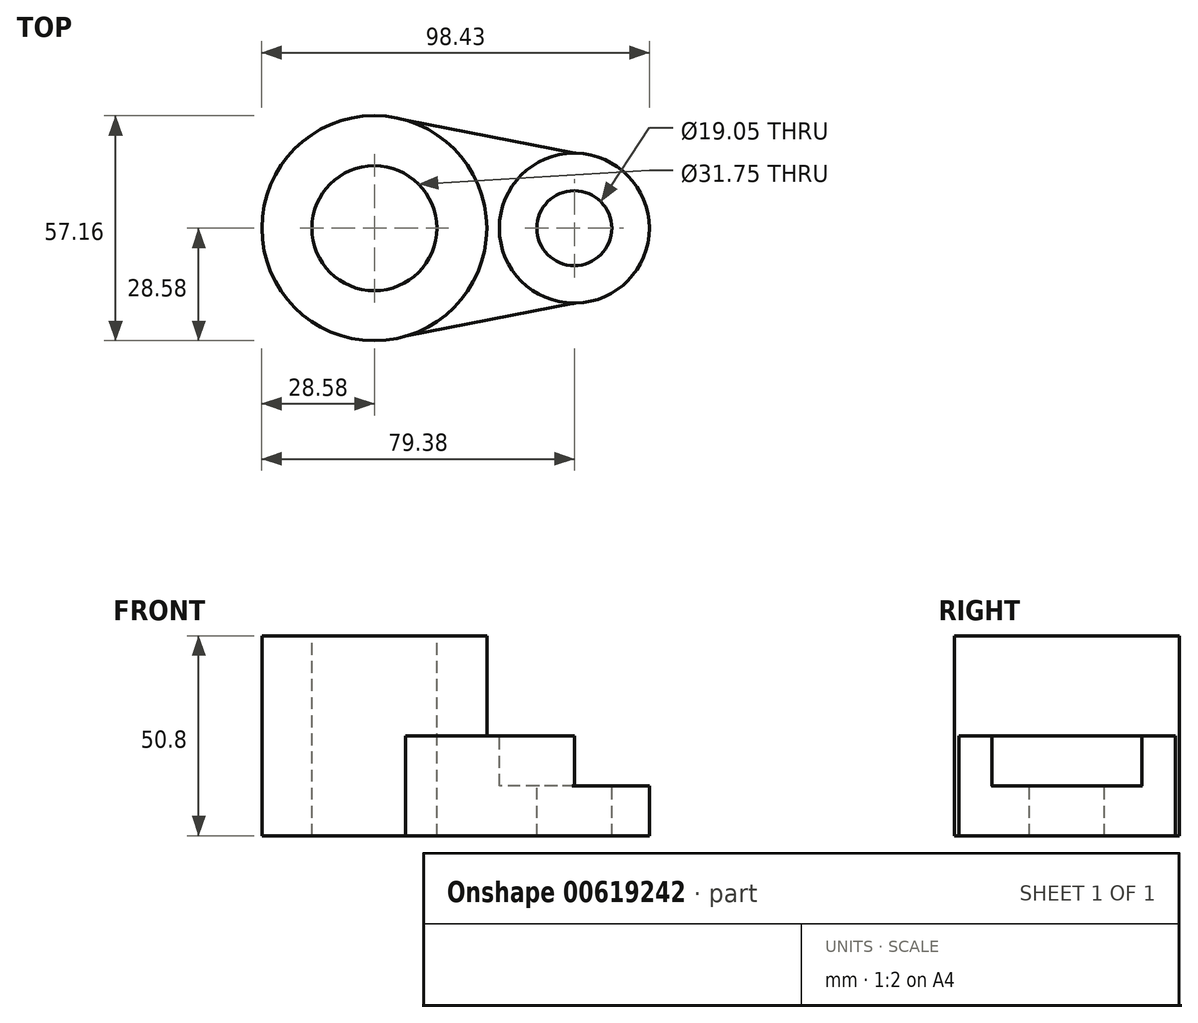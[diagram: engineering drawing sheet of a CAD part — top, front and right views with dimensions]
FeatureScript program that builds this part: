
annotation { "Feature Type Name" : "Feature", "Feature Type Description" : "" }
export const myFeature = defineFeature(function(context is Context, id is Id, definition is map)
    precondition{}
    {
        {
            var Q0;
            Q0=qCreatedBy(makeId("Top.planeOp"),FACE);
            var sketch = newSketch(context, id + "F0", { "sketchPlane" : qUnion([Q0])});
            skCircle(sketch, "E0", {"center": v(0, 0) * mm, "radius": 28.58 * mm});
            skCircle(sketch, "E1", {"center": v(0, 0) * mm, "radius": 15.88 * mm});
            skCircle(sketch, "E2", {"center": v(50.8, 0) * mm, "radius": 9.53 * mm});
            skCircle(sketch, "E3", {"center": v(50.8, 0) * mm, "radius": 19.05 * mm});
            skLineSegment(sketch, "E4", {"start": v(50.8, 19.05) * mm, "end": v(7.9, 27.46) * mm});
            skLineSegment(sketch, "E5", {"start": v(7.9, -27.46) * mm, "end": v(50.8, -19.05) * mm});
            skSolve(sketch);
        }
        {
            var Q0;
            Q0=makeQuery(id+"F0.imprint","IMPRINT",FACE,{"disambiguationData":[TD([[makeQuery(id+"F0.imprint","IMPRINT",EDGE,{"derivedFrom":sQuery(id+"F0.wireOp",EDGE,"E1")}),-1.0]])]});
            var Q1;
            {var subQ0=sQuery(id+"F0.wireOp",EDGE,"E4");Q1=makeQuery(id+"F0.imprint","IMPRINT",FACE,{"disambiguationData":[TD([[makeQuery(id+"F0.imprint","IMPRINT",EDGE,{"derivedFrom":subQ0}),1.0]])]});}
            var Q2;
            Q2=makeQuery(id+"F0.imprint","IMPRINT",FACE,{"disambiguationData":[TD([[makeQuery(id+"F0.imprint","IMPRINT",EDGE,{"derivedFrom":sQuery(id+"F0.wireOp",EDGE,"E2")}),-1.0]])]});
            extrude(context, id + "F1", {"entities" : qUnion([Q0, Q1, Q2]), "oppositeDirection" : true, "depth" : 25.4 * mm, "offsetDistance" : 25.4 * mm});
        }
        {
            var Q0;
            Q0=makeQuery(id+"F0.imprint","IMPRINT",FACE,{"disambiguationData":[TD([[makeQuery(id+"F0.imprint","IMPRINT",EDGE,{"derivedFrom":sQuery(id+"F0.wireOp",EDGE,"E1")}),-1.0]])]});
            extrude(context, id + "F2", {"entities" : qUnion([Q0]), "operationType" : NewBodyOperationType.ADD, "depth" : 25.4 * mm, "offsetDistance" : 25.4 * mm});
        }
        {
            var Q0;
            Q0=makeQuery(id+"F0.imprint","IMPRINT",FACE,{"disambiguationData":[TD([[makeQuery(id+"F0.imprint","IMPRINT",EDGE,{"derivedFrom":sQuery(id+"F0.wireOp",EDGE,"E2")}),-1.0]])]});
            extrude(context, id + "F3", {"entities" : qUnion([Q0]), "operationType" : NewBodyOperationType.REMOVE, "oppositeDirection" : true, "depth" : 12.7 * mm, "offsetDistance" : 25.4 * mm});
        }
        {
            var Q0;
            {var subQ0=sQuery(id+"F0.wireOp",EDGE,"E4");var subQ1=sQuery(id+"F0.wireOp",EDGE,"E3");Q0=makeQuery(id+"F3.boolean.opBoolean","SPLIT",EDGE,{"disambiguationData":[topologyDisambiguationEdgeConnected([makeQuery(id+"F3.opExtrude","SWEPT_FACE",FACE,{"disambiguationData":[OSD([subQ1])]})])],"derivedFrom":makeQuery(id+"F1.opExtrude","SWEPT_EDGE",EDGE,{"disambiguationData":[OSD([subQ1,subQ0])]})});}
            var Q1;
            {var subQ0=sQuery(id+"F0.wireOp",EDGE,"E5");var subQ1=sQuery(id+"F0.wireOp",EDGE,"E3");Q1=makeQuery(id+"F3.boolean.opBoolean","SPLIT",EDGE,{"disambiguationData":[topologyDisambiguationEdgeConnected([makeQuery(id+"F3.opExtrude","SWEPT_FACE",FACE,{"disambiguationData":[OSD([subQ1])]})])],"derivedFrom":makeQuery(id+"F1.opExtrude","SWEPT_EDGE",EDGE,{"disambiguationData":[OSD([subQ1,subQ0])]})});}
            fillet(context, id + "F4", {"entities" : qUnion([Q0, Q1]), "radius" : 6.35 * mm, "tangentPropagation" : true, "allowEdgeOverflow" : false});
        }
    });
